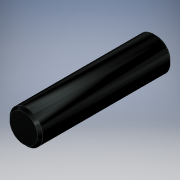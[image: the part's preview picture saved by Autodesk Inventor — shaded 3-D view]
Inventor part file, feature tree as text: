
AUTODESK INVENTOR PART (.ipt)
format: ipt  version: 2019.4 (Build 234330000, 330)  size: 110,592 bytes
history: native  units: in
note: dims shown in document units (in); Inventor stores cm internally (conversion verified against a paired STEP export)
features: extrude x1, chamfer x1, sketch x1
ambient origin geometry x8: Origin, YZ Plane, XZ Plane, XY Plane, X Axis, Y Axis, Z Axis, Center Point
bodies: Solid1 (feature_tree)
feature tree (3):
  extrude  "Extrusion1"  Depth=1.0in TaperAngle=0.0deg
  chamfer  "Chamfer1"  Distance=0.125in Angle=45.0deg
  sketch  "Sketch1"  dims[d0=0.25in d1=1.0in d2=0.0in d3=0.02in d4=0.125in d5=45.0deg]
